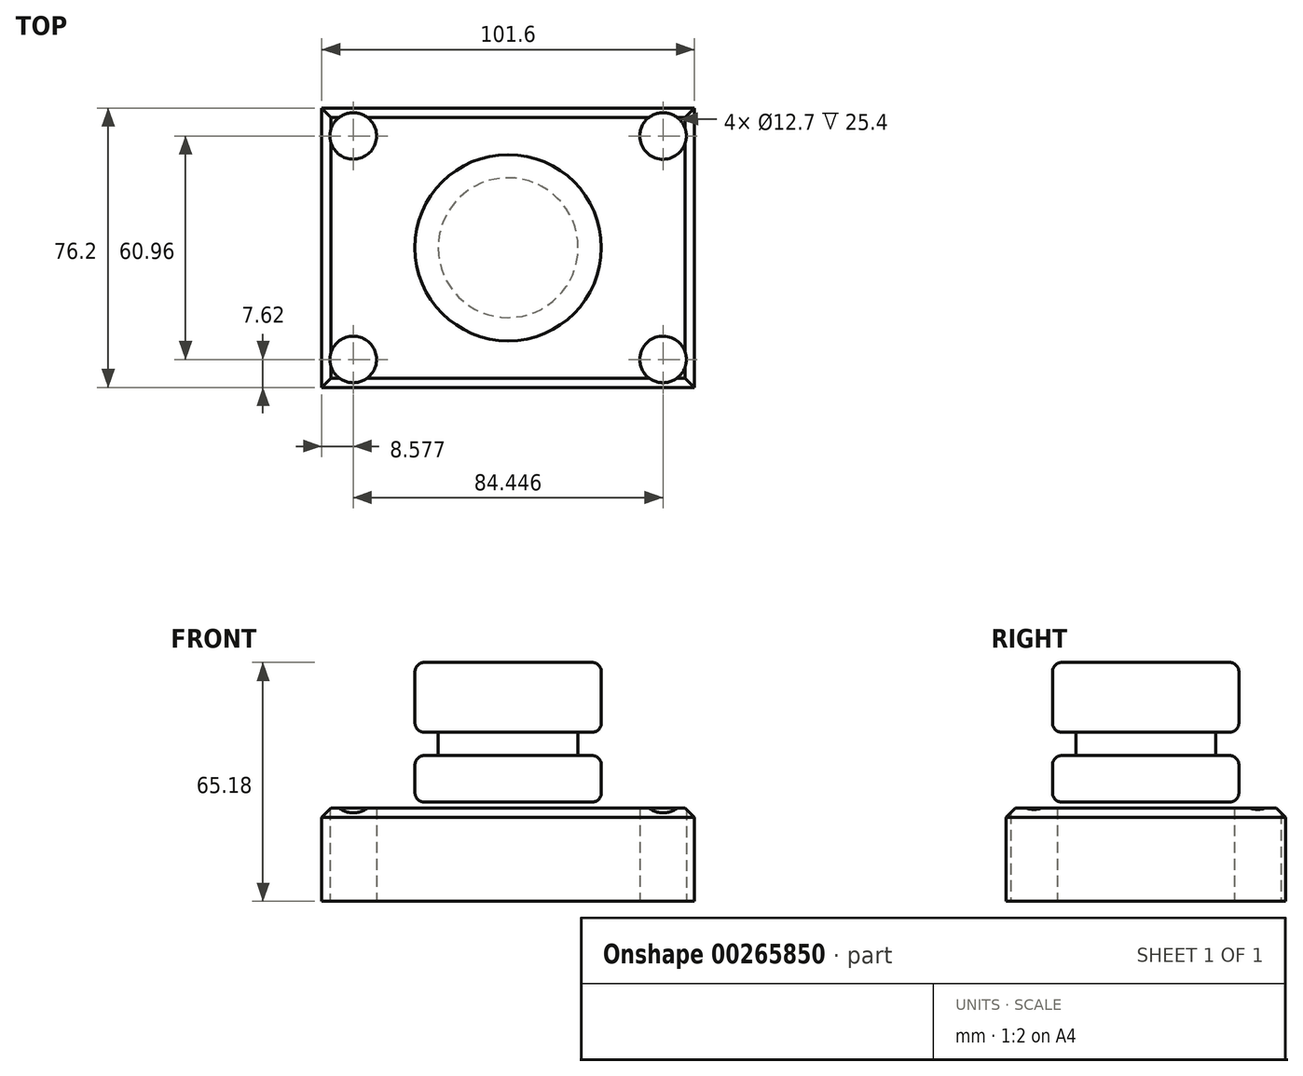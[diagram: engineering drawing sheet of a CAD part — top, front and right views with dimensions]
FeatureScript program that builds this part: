
annotation { "Feature Type Name" : "Feature", "Feature Type Description" : "" }
export const myFeature = defineFeature(function(context is Context, id is Id, definition is map)
    precondition{}
    {
        {
            var Q0;
            Q0=qCreatedBy(makeId("Top.planeOp"),FACE);
            var sketch = newSketch(context, id + "F0", { "sketchPlane" : qUnion([Q0])});
            skLineSegment(sketch, "E0.bottom", {"start": v(50.8, 38.1) * mm, "end": v(-50.8, 38.1) * mm});
            skLineSegment(sketch, "E0.top", {"start": v(50.8, -38.1) * mm, "end": v(-50.8, -38.1) * mm});
            skLineSegment(sketch, "E0.left", {"start": v(50.8, 38.1) * mm, "end": v(50.8, -38.1) * mm});
            skLineSegment(sketch, "E0.right", {"start": v(-50.8, 38.1) * mm, "end": v(-50.8, -38.1) * mm});
            skPoint(sketch, "E0.middle", {"position": v(0, 0) * mm});
            skSolve(sketch);
        }
        {
            var Q0;
            Q0=makeQuery(id+"F0.imprint","IMPRINT",FACE,{"disambiguationData":[TD([[makeQuery(id+"F0.imprint","IMPRINT",EDGE,{"derivedFrom":sQuery(id+"F0.wireOp",EDGE,"E0.bottom")}),1.0]])]});
            var Q1;
            Q1 = qSketchRegion(id + "F2", true);
            extrude(context, id + "F1", {"entities" : qUnion([Q0, Q1]), "depth" : 25.4 * mm});
        }
        {
            var Q0;
            Q0=makeQuery(id+"F1.opExtrude","CAP_FACE",FACE,{"disambiguationData":[OSD([sQuery(id+"F0.wireOp",EDGE,"E0.bottom"),sQuery(id+"F0.wireOp",EDGE,"E0.top"),sQuery(id+"F0.wireOp",EDGE,"E0.left"),sQuery(id+"F0.wireOp",EDGE,"E0.right")])],"isStart":true});
            var sketch = newSketch(context, id + "F2", { "sketchPlane" : qUnion([Q0])});
            skCircle(sketch, "E1", {"center": v(-42.22, 30.48) * mm, "radius": 6.35 * mm});
            skCircle(sketch, "E2", {"center": v(-42.22, -30.48) * mm, "radius": 6.35 * mm});
            skCircle(sketch, "E3", {"center": v(42.22, -30.48) * mm, "radius": 6.35 * mm});
            skCircle(sketch, "E4", {"center": v(42.22, 30.48) * mm, "radius": 6.35 * mm});
            skSolve(sketch);
        }
        {
            var Q0;
            Q0=makeQuery(id+"F2.imprint","IMPRINT",FACE,{"disambiguationData":[TD([[makeQuery(id+"F2.imprint","IMPRINT",EDGE,{"derivedFrom":sQuery(id+"F2.wireOp",EDGE,"E2")}),1.0]])]});
            var Q1;
            Q1=makeQuery(id+"F2.imprint","IMPRINT",FACE,{"disambiguationData":[TD([[makeQuery(id+"F2.imprint","IMPRINT",EDGE,{"derivedFrom":sQuery(id+"F2.wireOp",EDGE,"E1")}),1.0]])]});
            var Q2;
            Q2=makeQuery(id+"F2.imprint","IMPRINT",FACE,{"disambiguationData":[TD([[makeQuery(id+"F2.imprint","IMPRINT",EDGE,{"derivedFrom":sQuery(id+"F2.wireOp",EDGE,"E4")}),1.0]])]});
            var Q3;
            Q3=makeQuery(id+"F2.imprint","IMPRINT",FACE,{"disambiguationData":[TD([[makeQuery(id+"F2.imprint","IMPRINT",EDGE,{"derivedFrom":sQuery(id+"F2.wireOp",EDGE,"E3")}),1.0]])]});
            extrude(context, id + "F3", {"entities" : qUnion([Q0, Q1, Q2, Q3]), "operationType" : NewBodyOperationType.REMOVE, "oppositeDirection" : true, "depth" : 25.4 * mm});
        }
        {
            var Q0;
            Q0=qCreatedBy(makeId("Front.planeOp"),FACE);
            var sketch = newSketch(context, id + "F4", { "sketchPlane" : qUnion([Q0])});
            skLineSegment(sketch, "E5.bottom", {"start": v(0, 27.08) * mm, "end": v(-25.4, 27.08) * mm});
            skLineSegment(sketch, "E5.top", {"start": v(0, 65.18) * mm, "end": v(-25.4, 65.18) * mm});
            skLineSegment(sketch, "E5.left", {"start": v(0, 27.08) * mm, "end": v(0, 65.18) * mm});
            skLineSegment(sketch, "E5.right", {"start": v(-25.4, 27.08) * mm, "end": v(-25.4, 65.18) * mm});
            skSolve(sketch);
        }
        {
            var Q0;
            Q0=makeQuery(id+"F4.imprint","IMPRINT",FACE,{"disambiguationData":[TD([[makeQuery(id+"F4.imprint","IMPRINT",EDGE,{"derivedFrom":sQuery(id+"F4.wireOp",EDGE,"E5.bottom")}),-1.0]])]});
            var Q1;
            Q1=sQuery(id+"F4.wireOp",EDGE,"E5.left");
            revolve(context, id + "F5", {"entities" : qUnion([Q0]), "axis" : qUnion([Q1]), "revolveType" : RevolveType.FULL});
        }
        {
            var Q0;
            Q0=qCreatedBy(makeId("Right.planeOp"),FACE);
            var sketch = newSketch(context, id + "F6", { "sketchPlane" : qUnion([Q0])});
            skLineSegment(sketch, "E6.bottom", {"start": v(-19.05, 46.13) * mm, "end": v(-42.33, 46.13) * mm});
            skLineSegment(sketch, "E6.top", {"start": v(-19.05, 39.78) * mm, "end": v(-42.33, 39.78) * mm});
            skLineSegment(sketch, "E6.left", {"start": v(-19.05, 46.13) * mm, "end": v(-19.05, 39.78) * mm});
            skLineSegment(sketch, "E6.right", {"start": v(-42.33, 46.13) * mm, "end": v(-42.33, 39.78) * mm});
            skSolve(sketch);
        }
        {
            var Q0;
            Q0 = qSketchRegion(id + "F6", true);
            var Q1;
            Q1=makeQuery(id+"F5.opRevolve","SWEPT_FACE",FACE,{"disambiguationData":[OSD([sQuery(id+"F4.wireOp",EDGE,"E5.right")])]});
            revolve(context, id + "F7", {"operationType" : NewBodyOperationType.REMOVE, "entities" : qUnion([Q0]), "axis" : qUnion([Q1]), "revolveType" : RevolveType.FULL});
        }
        {
            var Q0;
            Q0=makeQuery(id+"F1.opExtrude","CAP_EDGE",EDGE,{"disambiguationData":[OSD([sQuery(id+"F0.wireOp",EDGE,"E0.top")])],"isStart":false});
            var Q1;
            Q1=makeQuery(id+"F1.opExtrude","CAP_EDGE",EDGE,{"disambiguationData":[OSD([sQuery(id+"F0.wireOp",EDGE,"E0.left")])],"isStart":false});
            var Q2;
            Q2=makeQuery(id+"F1.opExtrude","CAP_EDGE",EDGE,{"disambiguationData":[OSD([sQuery(id+"F0.wireOp",EDGE,"E0.bottom")])],"isStart":false});
            var Q3;
            Q3=makeQuery(id+"F1.opExtrude","CAP_EDGE",EDGE,{"disambiguationData":[OSD([sQuery(id+"F0.wireOp",EDGE,"E0.right")])],"isStart":false});
            chamfer(context, id + "F8", {"entities" : qUnion([Q0, Q1, Q2, Q3]), "width" : 2.54 * mm, "tangentPropagation" : true});
        }
        {
            var Q0;
            Q0=makeQuery(id+"F5.opRevolve","SWEPT_EDGE",EDGE,{"disambiguationData":[OSD([sQuery(id+"F4.wireOp",EDGE,"E5.bottom"),sQuery(id+"F4.wireOp",EDGE,"E5.right")])]});
            var Q1;
            Q1=makeQuery(id+"F7.boolean.opBoolean","INTERSECT",EDGE,{"derivedFrom":[makeQuery(id+"F5.opRevolve","SWEPT_FACE",FACE,{"disambiguationData":[OSD([sQuery(id+"F4.wireOp",EDGE,"E5.right")])]}),makeQuery(id+"F7.opRevolve","SWEPT_FACE",FACE,{"disambiguationData":[OSD([sQuery(id+"F6.wireOp",EDGE,"E6.top")])]})]});
            var Q2;
            Q2=makeQuery(id+"F7.boolean.opBoolean","INTERSECT",EDGE,{"derivedFrom":[makeQuery(id+"F5.opRevolve","SWEPT_FACE",FACE,{"disambiguationData":[OSD([sQuery(id+"F4.wireOp",EDGE,"E5.right")])]}),makeQuery(id+"F7.opRevolve","SWEPT_FACE",FACE,{"disambiguationData":[OSD([sQuery(id+"F6.wireOp",EDGE,"E6.bottom")])]})]});
            var Q3;
            Q3=makeQuery(id+"F5.opRevolve","SWEPT_EDGE",EDGE,{"disambiguationData":[OSD([sQuery(id+"F4.wireOp",EDGE,"E5.top"),sQuery(id+"F4.wireOp",EDGE,"E5.right")])]});
            fillet(context, id + "F9", {"entities" : qUnion([Q0, Q1, Q2, Q3]), "radius" : 2.54 * mm, "tangentPropagation" : true, "allowEdgeOverflow" : false});
        }
    });
